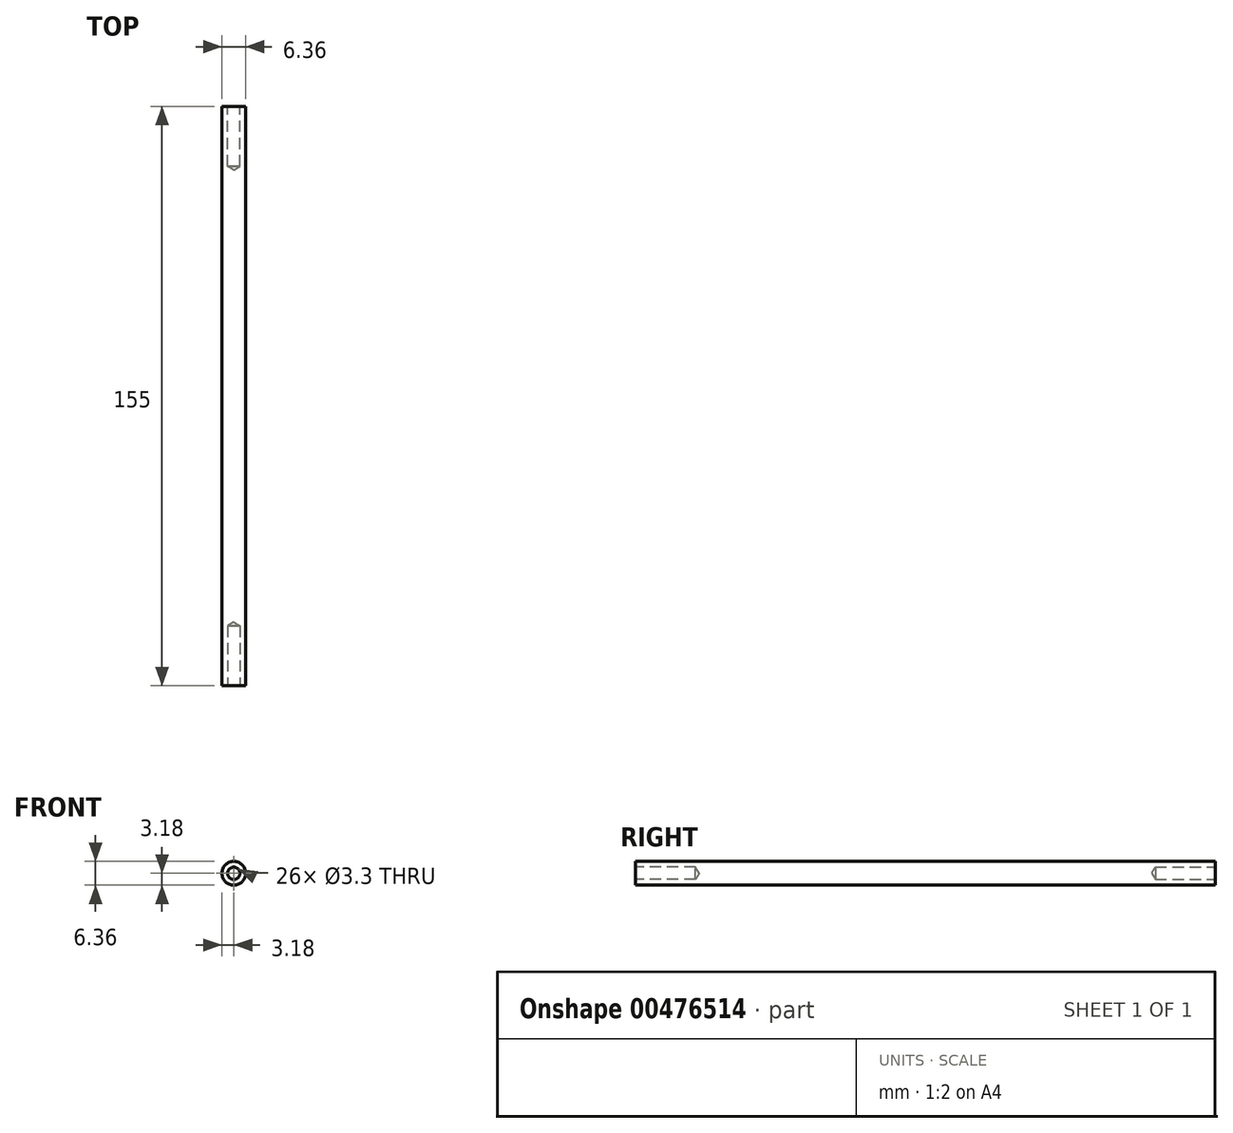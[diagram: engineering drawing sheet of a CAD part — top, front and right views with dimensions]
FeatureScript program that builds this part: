
annotation { "Feature Type Name" : "Feature", "Feature Type Description" : "" }
export const myFeature = defineFeature(function(context is Context, id is Id, definition is map)
    precondition{}
    {
        {
            var Q0;
            Q0=qCreatedBy(makeId("Front.planeOp"),FACE);
            var sketch = newSketch(context, id + "F0", { "sketchPlane" : qUnion([Q0])});
            skCircle(sketch, "E0", {"center": v(0, 0) * mm, "radius": 3.18 * mm});
            skSolve(sketch);
        }
        {
            var Q0;
            Q0=makeQuery(id+"F0.imprint","IMPRINT",FACE,{"disambiguationData":[TD([[makeQuery(id+"F0.imprint","IMPRINT",EDGE,{"derivedFrom":sQuery(id+"F0.wireOp",EDGE,"E0")}),1.0]])]});
            extrude(context, id + "F1", {"entities" : qUnion([Q0]), "depth" : 155 * mm});
        }
        {
            var Q0;
            Q0=sQuery(id+"F0.wireOp",VERTEX,"E0.center");
            var Q1;
            Q1=makeQuery(id+"F1.opExtrude","SWEPT_BODY",BODY,{"disambiguationData":[OSD([sQuery(id+"F0.wireOp",EDGE,"E0")])]});
            hole(context, id + "F2", {"style" : HoleStyle.SIMPLE, "endStyle" : HoleEndStyle.BLIND, "oppositeDirection" : true, "standardTappedOrClearance" : lookupTablePath({ "standard" : "ISO", "engagement" : "75%", "pitch" : "0.7 mm", "size" : "M4", "type" : "Tapped" }), "standardBlindInLast" : lookupTablePath({ "standard" : "ISO", "engagement" : "75%", "pitch" : "0.7 mm", "size" : "M4", "type" : "Tapped" }), "holeDiameter" : 3.3 * mm, "showTappedDepth" : true, "holeDepth" : 16 * mm, "tappedDepth" : 13.9 * mm, "tapClearance" : 3, "startFromSketch" : true, "locations" : qUnion([Q0]), "scope" : qUnion([Q1]), "majorDiameter" : 4 * mm});
        }
        {
            var Q0;
            Q0=makeQuery(id+"F1.opExtrude","CAP_FACE",FACE,{"disambiguationData":[OSD([sQuery(id+"F0.wireOp",EDGE,"E0")])],"isStart":false});
            var sketch = newSketch(context, id + "F3", { "sketchPlane" : qUnion([Q0])});
            skCircle(sketch, "E1.0.0", {"center": v(0, 0) * mm, "radius": 3.18 * mm});
            skSolve(sketch);
        }
        {
            var Q0;
            Q0=sQuery(id+"F3.wireOp",VERTEX,"E1.0.0.center");
            var Q1;
            Q1=makeQuery(id+"F1.opExtrude","SWEPT_BODY",BODY,{"disambiguationData":[OSD([sQuery(id+"F0.wireOp",EDGE,"E0")])]});
            hole(context, id + "F4", {"style" : HoleStyle.SIMPLE, "endStyle" : HoleEndStyle.BLIND, "standardTappedOrClearance" : lookupTablePath({ "standard" : "ISO", "engagement" : "75%", "pitch" : "0.7 mm", "size" : "M4", "type" : "Tapped" }), "standardBlindInLast" : lookupTablePath({ "standard" : "ISO", "engagement" : "75%", "pitch" : "0.7 mm", "size" : "M4", "type" : "Tapped" }), "holeDiameter" : 3.3 * mm, "showTappedDepth" : true, "holeDepth" : 16 * mm, "tappedDepth" : 13.9 * mm, "tapClearance" : 3, "startFromSketch" : true, "locations" : qUnion([Q0]), "scope" : qUnion([Q1]), "majorDiameter" : 4 * mm});
        }
    });
